# Revit family: 44780211
name_source: partatom
category: Plumbing Fixtures
units: mm (PartAtom-declared; Revit-internal decimal feet)

## family parameters
Always vertical = Yes
Cut with Voids When Loaded = No
OmniClass Number = 23.45.55.00
OmniClass Title = Sanitary Faucets, Wastes
Part Type = Normal
Room Calculation Point = No
Round Connector Dimension = Use Diameter
Shared = No
Work Plane-Based = No

## types (1)
- 44780211 Shower set
    2D/3D/BIM Files URL = http://static.hansa.com
    3D View = https://static.hansa.com
    AssetType = Fixed
    BIMObjectName = 44780211
    BodyMaterial = Brass
    Brand = HANSA
    Catalog Drawing URL = http://static.hansa.com
    Category = Shower solutions
    CloseOffRating = 0
    Color = Chrome
    Connection Size = G1/2
    DN Size = 18 mm
    Default Elevation = 0 mm  [stored 0 ft]
    Dimension Drawing URL = http://static.hansa.com
    DurationUnit = Year
    EAN Number = 4057304002458
    EN Standard = EN 1112, EN 1113
    ETIM Class Number = EC010109 Sliding rod combination
    FDV Document URL = http://www.hansa.com
    FaucetMainMaterial = Brass
    Finish = Polished
    Flow Drawing URL = http://static.hansa.com
    Flow Rate At 300kPa = 0.0 L/s
    Flow Rate At 300kPa With Flow Controller = 0.3 L/s
    FlowCoefficient = 0
    Group = Shower set
    Hand Shower Size = Ø 70 mm
    IfcExportAs = IfcValveType
    IfcExportType = FAUCET
    InletConnectionSize = 10 mm  [stored 0.0328084 ft]
    Installation Type = Wall mounted
    Installation and Maintenance Guide URL = http://static.hansa.com
    Interactive AR View URL = https://static.hansa.com
    Manufacturer = HANSA
    ManufacturerName = HANSA
    ManufacturerURL = http://www.hansa.com
    Market = Austria;Belgium;Czech Republic;Spain;France;International;Italy;Netherlands;Slovakia
    Material = Composite
    Max. Hot Water Supply = 65 °C
    Mobile Product Information URL = http://mpi.hansa.com
    Model = 44780211 Shower set
    ModelReference = 44780211
    NBSDescription = Shower mixers
    NBSReference = 45-35-70/335
    Name = 44780211 Shower set
    Name_en = 44780211 Shower set
    NominalDepth = 138 mm  [stored 0.452756 ft]
    NominalHeight = 701 mm  [stored 2.29987 ft]
    NominalWidth = 220 mm
    Product Code = 44780211
    Product Family = HANSABASICJET
    Product Image URL = http://static.hansa.com
    Product URL = http://static.hansa.com
    Sales Package dimensions (LxWxH) = 720.0 x 155.0 x 55.0
    Shape = Sculptured
    Shower Parts = Hand shower;Shower rail;Adjustable shower rail bracket;Soap dish;Shower hose (1500 mm);Anti limescale technology (easy to clean)
    Shower Spray = Relaxing
    Shower Spray Number = 1 shower spray
    Size = 220x138x701 mm
    Spare-Part Information URL = http://static.hansa.com
    Surface treatment = Chrome
    Technical DataSheet URL = http://www.hansa.com
    UNSPSC Class Number = 30181503 Showers
    URL Declaration Of Performance (DOP) = http://static.hansa.com
    URL Declaration of Asbestos = http://static.hansa.com
    URL Declaration of Conformity = http://static.hansa.com
    URL Declaration of SCIP = http://static.hansa.com
    URL EU Packaging Declaration = http://static.hansa.com
    URL EcoLabel Declaration = http://static.hansa.com
    URL REACH = http://static.hansa.com
    Uniclass2 = Pr_40_30_96_78
    Uniclass2015Description = Shower manual water supply sets
    Uniclass2015Reference = Pr_40_20_87_78
    Version = 1
    VersionDate = 01/06/2023
    Warranty Information URL = http://warranty.hansa.com
    WarrantyDescription = http://warranty.hansa.com
    WarrantyDurationUnit = Year
    Working Pressure = 50 - 500 kPa

note: [stored X ft] marks values corroborated as IEEE doubles in the binary element streams (Revit-internal decimal feet)

## geometry (parser evidence)
native form markers: Sweep x3
no freeform markers — native parametric forms only
